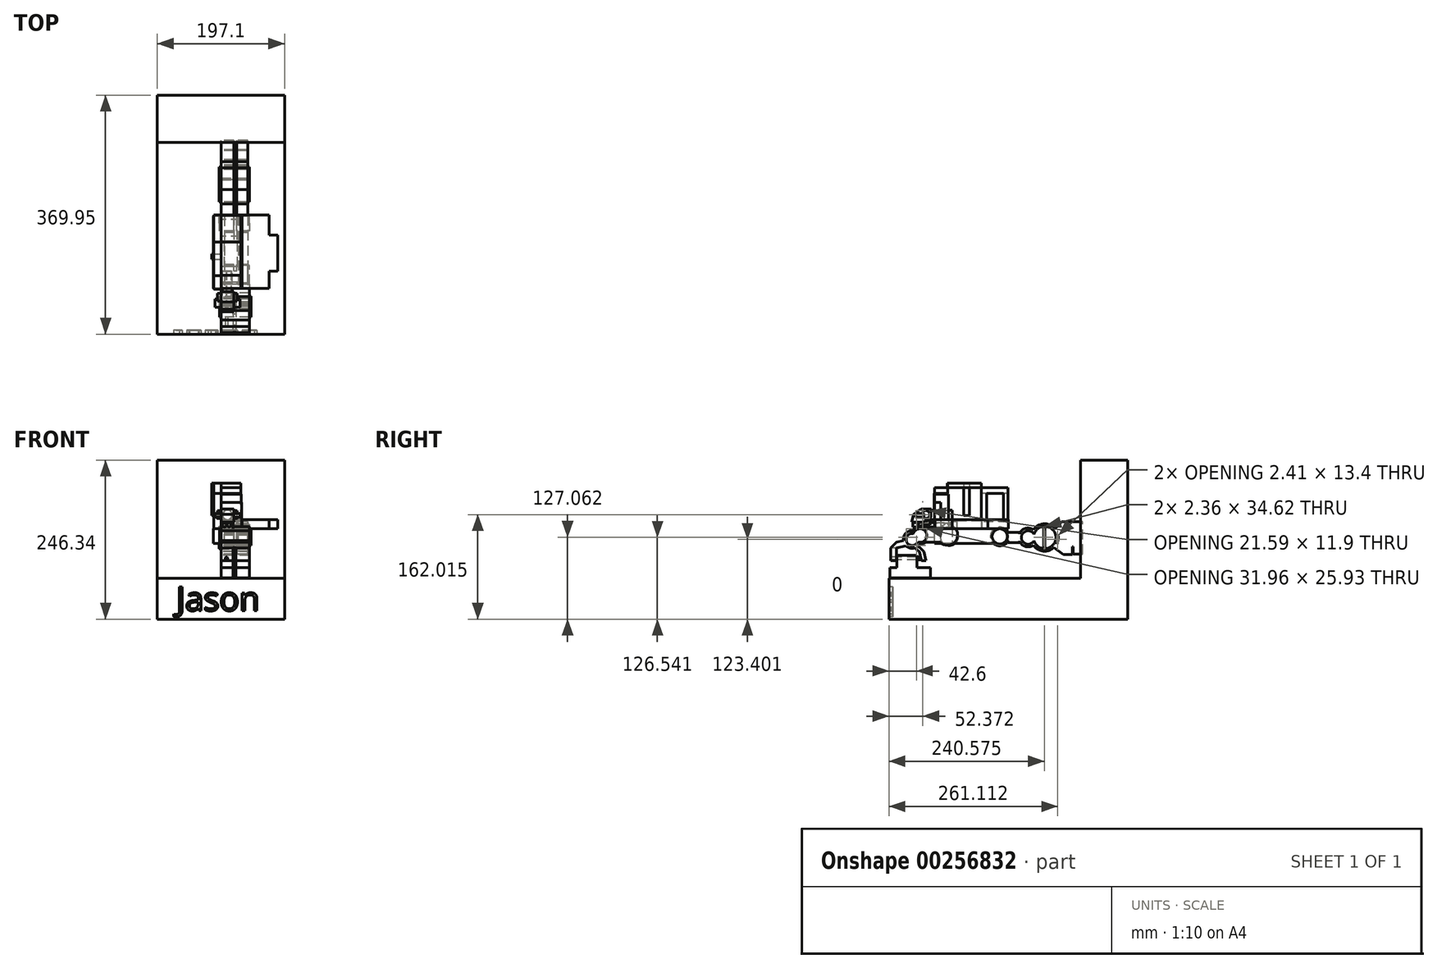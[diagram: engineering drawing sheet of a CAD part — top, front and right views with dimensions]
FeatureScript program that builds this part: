
annotation { "Feature Type Name" : "Feature", "Feature Type Description" : "" }
export const myFeature = defineFeature(function(context is Context, id is Id, definition is map)
    precondition{}
    {
        {
            var Q0;
            Q0=qCreatedBy(makeId("Right.planeOp"),FACE);
            var sketch = newSketch(context, id + "F0", { "sketchPlane" : qUnion([Q0])});
            skLineSegment(sketch, "E0", {"start": v(-32.05, 30.72) * mm, "end": v(-47.84, 30.72) * mm});
            skLineSegment(sketch, "E1", {"start": v(-47.84, 30.72) * mm, "end": v(-59.25, 22.22) * mm});
            skLineSegment(sketch, "E2", {"start": v(-59.25, 22.22) * mm, "end": v(-62.9, 10.56) * mm});
            skLineSegment(sketch, "E3", {"start": v(-62.9, 10.56) * mm, "end": v(-43.95, 10.56) * mm});
            skLineSegment(sketch, "E4", {"start": v(-43.95, 10.56) * mm, "end": v(-40.55, 13.23) * mm});
            skLineSegment(sketch, "E5", {"start": v(-40.55, 13.23) * mm, "end": v(-33.74, 13.23) * mm});
            skLineSegment(sketch, "E6", {"start": v(-33.74, 13.23) * mm, "end": v(-32.05, 30.72) * mm});
            skSolve(sketch);
        }
        {
            var Q0;
            Q0 = qSketchRegion(id + "F0", true);
            extrude(context, id + "F1", {"entities" : qUnion([Q0]), "depth" : 19.8 * mm});
        }
        {
            var Q0;
            Q0=qCreatedBy(makeId("Front.planeOp"),FACE);
            var sketch = newSketch(context, id + "F2", { "sketchPlane" : qUnion([Q0])});
            skCircle(sketch, "E7", {"center": v(9.48, 21.53) * mm, "radius": 7.5 * mm});
            skSolve(sketch);
        }
        {
            var Q0;
            Q0 = qSketchRegion(id + "F2", true);
            extrude(context, id + "F3", {"entities" : qUnion([Q0]), "operationType" : NewBodyOperationType.ADD, "depth" : 37.85 * mm});
        }
        {
            var Q0;
            Q0=qCreatedBy(makeId("Right.planeOp"),FACE);
            var sketch = newSketch(context, id + "F4", { "sketchPlane" : qUnion([Q0])});
            skLineSegment(sketch, "E8.bottom", {"start": v(-17.62, 40.64) * mm, "end": v(-27.05, 40.64) * mm});
            skLineSegment(sketch, "E8.top", {"start": v(-17.62, 0) * mm, "end": v(-27.05, 0) * mm});
            skLineSegment(sketch, "E8.left", {"start": v(-17.62, 40.64) * mm, "end": v(-17.62, 0) * mm});
            skLineSegment(sketch, "E8.right", {"start": v(-27.05, 40.64) * mm, "end": v(-27.05, 0) * mm});
            skSolve(sketch);
        }
        {
            var Q0;
            Q0 = qSketchRegion(id + "F4", true);
            extrude(context, id + "F5", {"entities" : qUnion([Q0]), "operationType" : NewBodyOperationType.ADD, "depth" : 31.5 * mm});
        }
        {
            var Q0;
            Q0=qCreatedBy(makeId("Top.planeOp"),FACE);
            var sketch = newSketch(context, id + "F6", { "sketchPlane" : qUnion([Q0])});
            skLineSegment(sketch, "E9.bottom", {"start": v(31.64, -17.62) * mm, "end": v(0, -17.62) * mm});
            skLineSegment(sketch, "E9.top", {"start": v(31.64, 7.04) * mm, "end": v(0, 7.04) * mm});
            skLineSegment(sketch, "E9.left", {"start": v(31.64, -17.62) * mm, "end": v(31.64, 7.04) * mm});
            skLineSegment(sketch, "E9.right", {"start": v(0, -17.62) * mm, "end": v(0, 7.04) * mm});
            skSolve(sketch);
        }
        {
            var Q0;
            Q0 = qSketchRegion(id + "F6", true);
            extrude(context, id + "F7", {"entities" : qUnion([Q0]), "operationType" : NewBodyOperationType.ADD, "depth" : 13.2 * mm});
        }
        {
            var Q0;
            Q0=qCreatedBy(makeId("Top.planeOp"),FACE);
            var sketch = newSketch(context, id + "F8", { "sketchPlane" : qUnion([Q0])});
            skLineSegment(sketch, "E10.bottom", {"start": v(31.4, 7.04) * mm, "end": v(25.12, 7.04) * mm});
            skLineSegment(sketch, "E10.top", {"start": v(31.4, 45.73) * mm, "end": v(25.12, 45.73) * mm});
            skLineSegment(sketch, "E10.left", {"start": v(31.4, 7.04) * mm, "end": v(31.4, 45.73) * mm});
            skLineSegment(sketch, "E10.right", {"start": v(25.12, 7.04) * mm, "end": v(25.12, 45.73) * mm});
            skSolve(sketch);
        }
        {
            var Q0;
            Q0 = qSketchRegion(id + "F8", true);
            extrude(context, id + "F9", {"entities" : qUnion([Q0]), "operationType" : NewBodyOperationType.ADD, "depth" : 12.95 * mm});
        }
        {
            var Q0;
            Q0=qCreatedBy(makeId("Top.planeOp"),FACE);
            var sketch = newSketch(context, id + "F10", { "sketchPlane" : qUnion([Q0])});
            skLineSegment(sketch, "E11.bottom", {"start": v(0, 7.28) * mm, "end": v(5.05, 7.28) * mm});
            skLineSegment(sketch, "E11.top", {"start": v(0, 46.45) * mm, "end": v(5.05, 46.45) * mm});
            skLineSegment(sketch, "E11.left", {"start": v(0, 7.28) * mm, "end": v(0, 46.45) * mm});
            skLineSegment(sketch, "E11.right", {"start": v(5.05, 7.28) * mm, "end": v(5.05, 46.45) * mm});
            skSolve(sketch);
        }
        {
            var Q0;
            Q0 = qSketchRegion(id + "F10", true);
            extrude(context, id + "F11", {"entities" : qUnion([Q0]), "depth" : 12.95 * mm});
        }
        {
            var Q0;
            Q0=qCreatedBy(makeId("Top.planeOp"),FACE);
            var sketch = newSketch(context, id + "F12", { "sketchPlane" : qUnion([Q0])});
            skLineSegment(sketch, "E12.bottom", {"start": v(31.16, 45.97) * mm, "end": v(0, 45.97) * mm});
            skLineSegment(sketch, "E12.top", {"start": v(31.16, 86.8) * mm, "end": v(0, 86.8) * mm});
            skLineSegment(sketch, "E12.left", {"start": v(31.16, 45.97) * mm, "end": v(31.16, 86.8) * mm});
            skLineSegment(sketch, "E12.right", {"start": v(0, 45.97) * mm, "end": v(0, 86.8) * mm});
            skSolve(sketch);
        }
        {
            var Q0;
            Q0 = qSketchRegion(id + "F12", true);
            extrude(context, id + "F13", {"entities" : qUnion([Q0]), "operationType" : NewBodyOperationType.ADD, "depth" : 13.97 * mm});
        }
        {
            var Q0;
            Q0=qCreatedBy(makeId("Top.planeOp"),FACE);
            var sketch = newSketch(context, id + "F14", { "sketchPlane" : qUnion([Q0])});
            skLineSegment(sketch, "E13.bottom", {"start": v(31.93, -26.75) * mm, "end": v(73.94, -26.75) * mm});
            skLineSegment(sketch, "E13.top", {"start": v(31.93, 86.9) * mm, "end": v(73.94, 86.9) * mm});
            skLineSegment(sketch, "E13.left", {"start": v(31.93, -26.75) * mm, "end": v(31.93, 86.9) * mm});
            skLineSegment(sketch, "E13.right", {"start": v(73.94, -26.75) * mm, "end": v(73.94, 86.9) * mm});
            skLineSegment(sketch, "E14.bottom", {"start": v(31.93, 0) * mm, "end": v(87.42, 0) * mm});
            skLineSegment(sketch, "E14.top", {"start": v(31.93, 55.68) * mm, "end": v(87.42, 55.68) * mm});
            skLineSegment(sketch, "E14.left", {"start": v(31.93, 0) * mm, "end": v(31.93, 55.68) * mm});
            skLineSegment(sketch, "E14.right", {"start": v(87.42, 0) * mm, "end": v(87.42, 55.68) * mm});
            skSolve(sketch);
        }
        {
            var Q0;
            Q0 = qSketchRegion(id + "F14", true);
            extrude(context, id + "F15", {"entities" : qUnion([Q0]), "depth" : 14.22 * mm});
        }
        {
            var Q0;
            Q0=qCreatedBy(makeId("Right.planeOp"),FACE);
            var sketch = newSketch(context, id + "F16", { "sketchPlane" : qUnion([Q0])});
            skLineSegment(sketch, "E15.bottom", {"start": v(86.49, 0) * mm, "end": v(-27.86, 0) * mm});
            skLineSegment(sketch, "E15.top", {"start": v(86.49, 54.6) * mm, "end": v(-27.86, 54.6) * mm});
            skLineSegment(sketch, "E15.left", {"start": v(86.49, 0) * mm, "end": v(86.49, 54.6) * mm});
            skLineSegment(sketch, "E15.right", {"start": v(-27.86, 0) * mm, "end": v(-27.86, 54.6) * mm});
            skLineSegment(sketch, "E16.bottom", {"start": v(45.18, 0) * mm, "end": v(-7.2, 0) * mm});
            skLineSegment(sketch, "E16.top", {"start": v(45.18, 70.73) * mm, "end": v(-7.2, 70.73) * mm});
            skLineSegment(sketch, "E16.left", {"start": v(45.18, 0) * mm, "end": v(45.18, 70.73) * mm});
            skLineSegment(sketch, "E16.right", {"start": v(-7.2, 0) * mm, "end": v(-7.2, 70.73) * mm});
            skSolve(sketch);
        }
        {
            var Q0;
            Q0 = qSketchRegion(id + "F16", true);
            extrude(context, id + "F17", {"entities" : qUnion([Q0]), "oppositeDirection" : true, "depth" : 11.43 * mm});
        }
        {
            var Q0;
            Q0=qCreatedBy(makeId("Top.planeOp"),FACE);
            var sketch = newSketch(context, id + "F18", { "sketchPlane" : qUnion([Q0])});
            skLineSegment(sketch, "E17.bottom", {"start": v(0, -5.7) * mm, "end": v(31, -5.7) * mm});
            skLineSegment(sketch, "E17.top", {"start": v(0, -26.85) * mm, "end": v(31, -26.85) * mm});
            skLineSegment(sketch, "E17.left", {"start": v(0, -5.7) * mm, "end": v(0, -26.85) * mm});
            skLineSegment(sketch, "E17.right", {"start": v(31, -5.7) * mm, "end": v(31, -26.85) * mm});
            skSolve(sketch);
        }
        {
            var Q0;
            Q0 = qSketchRegion(id + "F18", true);
            extrude(context, id + "F19", {"entities" : qUnion([Q0]), "depth" : 53.6 * mm});
        }
        {
            var Q0;
            Q0=qCreatedBy(makeId("Right.planeOp"),FACE);
            var sketch = newSketch(context, id + "F20", { "sketchPlane" : qUnion([Q0])});
            skLineSegment(sketch, "E18.bottom", {"start": v(45.1, 14.3) * mm, "end": v(53.66, 14.3) * mm});
            skLineSegment(sketch, "E18.top", {"start": v(45.1, 54.6) * mm, "end": v(53.66, 54.6) * mm});
            skLineSegment(sketch, "E18.left", {"start": v(45.1, 14.3) * mm, "end": v(45.1, 54.6) * mm});
            skLineSegment(sketch, "E18.right", {"start": v(53.66, 14.3) * mm, "end": v(53.66, 54.6) * mm});
            skLineSegment(sketch, "E19.bottom", {"start": v(79.86, 13.8) * mm, "end": v(86.4, 13.8) * mm});
            skLineSegment(sketch, "E19.top", {"start": v(79.86, 54.6) * mm, "end": v(86.4, 54.6) * mm});
            skLineSegment(sketch, "E19.left", {"start": v(79.86, 13.8) * mm, "end": v(79.86, 54.6) * mm});
            skLineSegment(sketch, "E19.right", {"start": v(86.4, 13.8) * mm, "end": v(86.4, 54.6) * mm});
            skLineSegment(sketch, "E20.bottom", {"start": v(86.4, 54.6) * mm, "end": v(45.1, 54.6) * mm});
            skLineSegment(sketch, "E20.top", {"start": v(86.4, 63.68) * mm, "end": v(45.1, 63.68) * mm});
            skLineSegment(sketch, "E20.left", {"start": v(86.4, 54.6) * mm, "end": v(86.4, 63.68) * mm});
            skLineSegment(sketch, "E20.right", {"start": v(45.1, 54.6) * mm, "end": v(45.1, 63.68) * mm});
            skLineSegment(sketch, "E21.bottom", {"start": v(45.1, 63.68) * mm, "end": v(-6.78, 63.68) * mm});
            skLineSegment(sketch, "E21.top", {"start": v(45.1, 70.73) * mm, "end": v(-6.78, 70.73) * mm});
            skLineSegment(sketch, "E21.left", {"start": v(45.1, 63.68) * mm, "end": v(45.1, 70.73) * mm});
            skLineSegment(sketch, "E21.right", {"start": v(-6.78, 63.68) * mm, "end": v(-6.78, 70.73) * mm});
            skLineSegment(sketch, "E22.bottom", {"start": v(-6.78, 63.68) * mm, "end": v(-26.93, 63.68) * mm});
            skLineSegment(sketch, "E22.top", {"start": v(-6.78, 54.6) * mm, "end": v(-26.93, 54.6) * mm});
            skLineSegment(sketch, "E22.left", {"start": v(-6.78, 63.68) * mm, "end": v(-6.78, 54.6) * mm});
            skLineSegment(sketch, "E22.right", {"start": v(-26.93, 63.68) * mm, "end": v(-26.93, 54.6) * mm});
            skSolve(sketch);
        }
        {
            var Q0;
            Q0 = qSketchRegion(id + "F20", true);
            extrude(context, id + "F21", {"entities" : qUnion([Q0]), "depth" : 30.23 * mm});
        }
        {
            var Q0;
            Q0=qCreatedBy(makeId("Top.planeOp"),FACE);
            var sketch = newSketch(context, id + "F22", { "sketchPlane" : qUnion([Q0])});
            skLineSegment(sketch, "E23.bottom", {"start": v(4.64, 84.64) * mm, "end": v(-12.48, 84.64) * mm});
            skLineSegment(sketch, "E23.top", {"start": v(4.64, -27.2) * mm, "end": v(-12.48, -27.2) * mm});
            skLineSegment(sketch, "E23.left", {"start": v(4.64, 84.64) * mm, "end": v(4.64, -27.2) * mm});
            skLineSegment(sketch, "E23.right", {"start": v(-12.48, 84.64) * mm, "end": v(-12.48, -27.2) * mm});
            skLineSegment(sketch, "E24.bottom", {"start": v(41.42, 85.14) * mm, "end": v(26.3, 85.14) * mm});
            skLineSegment(sketch, "E24.top", {"start": v(41.42, -27.2) * mm, "end": v(26.3, -27.2) * mm});
            skLineSegment(sketch, "E24.left", {"start": v(41.42, 85.14) * mm, "end": v(41.42, -27.2) * mm});
            skLineSegment(sketch, "E24.right", {"start": v(26.3, 85.14) * mm, "end": v(26.3, -27.2) * mm});
            skSolve(sketch);
        }
        {
            var Q0;
            Q0 = qSketchRegion(id + "F22", true);
            extrude(context, id + "F23", {"entities" : qUnion([Q0]), "oppositeDirection" : true, "depth" : 22.86 * mm});
        }
        {
            var Q0;
            Q0=qCreatedBy(makeId("Right.planeOp"),FACE);
            var sketch = newSketch(context, id + "F24", { "sketchPlane" : qUnion([Q0])});
            skLineSegment(sketch, "E25", {"start": v(-33.9, 12.8) * mm, "end": v(-33.9, 5.75) * mm});
            skLineSegment(sketch, "E26", {"start": v(-33.9, 5.75) * mm, "end": v(-47, 5.75) * mm});
            skLineSegment(sketch, "E27", {"start": v(-47, 5.75) * mm, "end": v(-52.04, 0) * mm});
            skLineSegment(sketch, "E28", {"start": v(-52.04, 0) * mm, "end": v(-52.04, 10.78) * mm});
            skLineSegment(sketch, "E29", {"start": v(-52.04, 10.78) * mm, "end": v(-33.9, 12.8) * mm});
            skSolve(sketch);
        }
        {
            var Q0;
            Q0 = qSketchRegion(id + "F24", true);
            extrude(context, id + "F25", {"entities" : qUnion([Q0]), "operationType" : NewBodyOperationType.ADD, "depth" : 18.29 * mm});
        }
        {
            var Q0;
            Q0=qCreatedBy(makeId("Right.planeOp"),FACE);
            var sketch = newSketch(context, id + "F26", { "sketchPlane" : qUnion([Q0])});
            skCircle(sketch, "E30", {"center": v(73.9, -11.89) * mm, "radius": 14.4 * mm});
            skCircle(sketch, "E31", {"center": v(-4.19, -11.38) * mm, "radius": 14.32 * mm});
            skLineSegment(sketch, "E32.bottom", {"start": v(86.78, -5.45) * mm, "end": v(104.12, -5.45) * mm});
            skLineSegment(sketch, "E32.top", {"start": v(86.78, -21.46) * mm, "end": v(104.12, -21.46) * mm});
            skLineSegment(sketch, "E32.left", {"start": v(86.78, -5.45) * mm, "end": v(86.78, -21.46) * mm});
            skLineSegment(sketch, "E32.right", {"start": v(104.12, -5.45) * mm, "end": v(104.12, -21.46) * mm});
            skCircle(sketch, "E33", {"center": v(117.72, -13.45) * mm, "radius": 14.62 * mm});
            skPoint(sketch, "E33.centerSnap0", {"position": v(104.12, -13.45) * mm});
            skCircle(sketch, "E34", {"center": v(143.41, -13.45) * mm, "radius": 21.13 * mm});
            skPoint(sketch, "E34.centerSnap0", {"position": v(86.78, -13.45) * mm});
            skLineSegment(sketch, "E35", {"start": v(159.7, 0) * mm, "end": v(169.6, 11.29) * mm});
            skLineSegment(sketch, "E36", {"start": v(169.6, 11.29) * mm, "end": v(187.74, 11.29) * mm});
            skLineSegment(sketch, "E37", {"start": v(187.74, 11.29) * mm, "end": v(187.74, 0) * mm});
            skLineSegment(sketch, "E38", {"start": v(187.74, 0) * mm, "end": v(171.12, 3) * mm});
            skLineSegment(sketch, "E39", {"start": v(171.12, 3) * mm, "end": v(164.23, -9.85) * mm});
            skLineSegment(sketch, "E40", {"start": v(164.23, -9.85) * mm, "end": v(162.13, -23.25) * mm});
            skLineSegment(sketch, "E41", {"start": v(162.13, -23.25) * mm, "end": v(173.63, -30.02) * mm});
            skLineSegment(sketch, "E42", {"start": v(173.63, -30.02) * mm, "end": v(186.17, -28.02) * mm});
            skLineSegment(sketch, "E43", {"start": v(186.17, -28.02) * mm, "end": v(186.17, -39.6) * mm});
            skLineSegment(sketch, "E44", {"start": v(186.17, -39.6) * mm, "end": v(172.63, -39.6) * mm});
            skLineSegment(sketch, "E45", {"start": v(172.63, -39.6) * mm, "end": v(157.55, -29.15) * mm});
            skLineSegment(sketch, "E46", {"start": v(157.55, -29.15) * mm, "end": v(159.7, 0) * mm});
            skLineSegment(sketch, "E47.bottom", {"start": v(187.74, 0) * mm, "end": v(173.63, 0) * mm});
            skLineSegment(sketch, "E47.top", {"start": v(187.74, -28.02) * mm, "end": v(173.63, -28.02) * mm});
            skLineSegment(sketch, "E47.left", {"start": v(187.74, 0) * mm, "end": v(187.74, -28.02) * mm});
            skLineSegment(sketch, "E47.right", {"start": v(173.63, 0) * mm, "end": v(173.63, -28.02) * mm});
            skLineSegment(sketch, "E48.bottom", {"start": v(187.74, 11.29) * mm, "end": v(202.35, 11.29) * mm});
            skLineSegment(sketch, "E48.top", {"start": v(187.74, -39.09) * mm, "end": v(202.35, -39.09) * mm});
            skLineSegment(sketch, "E48.left", {"start": v(187.74, 11.29) * mm, "end": v(187.74, -39.09) * mm});
            skLineSegment(sketch, "E48.right", {"start": v(202.35, 11.29) * mm, "end": v(202.35, -39.09) * mm});
            skSolve(sketch);
        }
        {
            var Q0;
            Q0 = qSketchRegion(id + "F26", true);
            extrude(context, id + "F27", {"entities" : qUnion([Q0]), "depth" : 40.9 * mm});
        }
        {
            var Q0;
            Q0=qCreatedBy(makeId("Right.planeOp"),FACE);
            var sketch = newSketch(context, id + "F28", { "sketchPlane" : qUnion([Q0])});
            skCircle(sketch, "E49", {"center": v(-7.37, -9.37) * mm, "radius": 16.03 * mm});
            skLineSegment(sketch, "E50.bottom", {"start": v(-20.39, 0) * mm, "end": v(-39.61, 0) * mm});
            skLineSegment(sketch, "E50.top", {"start": v(-20.39, -20.95) * mm, "end": v(-39.61, -20.95) * mm});
            skLineSegment(sketch, "E50.left", {"start": v(-20.39, 0) * mm, "end": v(-20.39, -20.95) * mm});
            skLineSegment(sketch, "E50.right", {"start": v(-39.61, 0) * mm, "end": v(-39.61, -20.95) * mm});
            skCircle(sketch, "E51", {"center": v(-49.69, -10.48) * mm, "radius": 13.58 * mm});
            skPoint(sketch, "E51.centerSnap0", {"position": v(-39.61, -10.48) * mm});
            skCircle(sketch, "E52", {"center": v(-61.86, -16.5) * mm, "radius": 13.76 * mm});
            skLineSegment(sketch, "E53", {"start": v(-52.57, -26.65) * mm, "end": v(-43.64, -35.56) * mm});
            skLineSegment(sketch, "E54", {"start": v(-43.64, -35.56) * mm, "end": v(-40.67, -49.28) * mm});
            skLineSegment(sketch, "E55", {"start": v(-40.67, -49.28) * mm, "end": v(-47.67, -49.28) * mm});
            skLineSegment(sketch, "E56", {"start": v(-47.67, -49.28) * mm, "end": v(-50.65, -35.56) * mm});
            skLineSegment(sketch, "E57", {"start": v(-50.65, -35.56) * mm, "end": v(-58.01, -29.7) * mm});
            skLineSegment(sketch, "E58", {"start": v(-75.48, -18.38) * mm, "end": v(-85.96, -20.65) * mm});
            skLineSegment(sketch, "E59", {"start": v(-85.96, -20.65) * mm, "end": v(-95.33, -29.7) * mm});
            skLineSegment(sketch, "E60", {"start": v(-95.33, -29.7) * mm, "end": v(-95.33, -49.28) * mm});
            skLineSegment(sketch, "E61", {"start": v(-95.33, -49.28) * mm, "end": v(-85.96, -49.28) * mm});
            skLineSegment(sketch, "E62", {"start": v(-85.96, -49.28) * mm, "end": v(-85.96, -35.56) * mm});
            skLineSegment(sketch, "E63", {"start": v(-85.96, -35.56) * mm, "end": v(-85.96, -29.7) * mm});
            skLineSegment(sketch, "E64", {"start": v(-85.96, -29.7) * mm, "end": v(-71.28, -26.52) * mm});
            skLineSegment(sketch, "E65.bottom", {"start": v(-54.73, -41.1) * mm, "end": v(-85.45, -41.1) * mm});
            skLineSegment(sketch, "E65.top", {"start": v(-54.73, -60.24) * mm, "end": v(-85.45, -60.24) * mm});
            skLineSegment(sketch, "E65.left", {"start": v(-54.73, -41.1) * mm, "end": v(-54.73, -60.24) * mm});
            skLineSegment(sketch, "E65.right", {"start": v(-85.45, -41.1) * mm, "end": v(-85.45, -60.24) * mm});
            skLineSegment(sketch, "E66.bottom", {"start": v(-33.57, -60.24) * mm, "end": v(-96.03, -60.24) * mm});
            skLineSegment(sketch, "E66.top", {"start": v(-33.57, -75.86) * mm, "end": v(-96.03, -75.86) * mm});
            skLineSegment(sketch, "E66.left", {"start": v(-33.57, -60.24) * mm, "end": v(-33.57, -75.86) * mm});
            skLineSegment(sketch, "E66.right", {"start": v(-96.03, -60.24) * mm, "end": v(-96.03, -75.86) * mm});
            skSolve(sketch);
        }
        {
            var Q0;
            Q0 = qSketchRegion(id + "F28", true);
            extrude(context, id + "F29", {"entities" : qUnion([Q0]), "depth" : 43.43 * mm});
        }
        {
            var Q0;
            Q0=qCreatedBy(makeId("Front.planeOp"),FACE);
            var sketch = newSketch(context, id + "F30", { "sketchPlane" : qUnion([Q0])});
            skCircle(sketch, "E67", {"center": v(4.88, 5.95) * mm, "radius": 3.27 * mm});
            skCircle(sketch, "E68", {"center": v(12.17, 6.2) * mm, "radius": 3.24 * mm});
            skSolve(sketch);
        }
        {
            var Q0;
            Q0 = qSketchRegion(id + "F30", true);
            extrude(context, id + "F31", {"entities" : qUnion([Q0]), "depth" : 60.45 * mm});
        }
        {
            var Q0;
            Q0=qCreatedBy(makeId("Right.planeOp"),FACE);
            var sketch = newSketch(context, id + "F32", { "sketchPlane" : qUnion([Q0])});
            skCircle(sketch, "E69", {"center": v(-40.48, 22) * mm, "radius": 6.02 * mm});
            skSolve(sketch);
        }
        {
            var Q0;
            Q0 = qSketchRegion(id + "F32", true);
            extrude(context, id + "F33", {"entities" : qUnion([Q0]), "operationType" : NewBodyOperationType.ADD, "depth" : 24.38 * mm, "hasSecondDirection" : true, "secondDirectionOppositeDirection" : true, "secondDirectionDepth" : 6.1 * mm});
        }
        {
            var Q0;
            Q0=qCreatedBy(makeId("Right.planeOp"),FACE);
            var sketch = newSketch(context, id + "F34", { "sketchPlane" : qUnion([Q0])});
            skLineSegment(sketch, "E70.bottom", {"start": v(-43.3, 23.51) * mm, "end": v(-56.2, 23.51) * mm});
            skLineSegment(sketch, "E70.top", {"start": v(-43.3, 18.14) * mm, "end": v(-56.2, 18.14) * mm});
            skLineSegment(sketch, "E70.left", {"start": v(-43.3, 23.51) * mm, "end": v(-43.3, 18.14) * mm});
            skLineSegment(sketch, "E70.right", {"start": v(-56.2, 23.51) * mm, "end": v(-56.2, 18.14) * mm});
            skSolve(sketch);
        }
        {
            var Q0;
            Q0 = qSketchRegion(id + "F34", true);
            extrude(context, id + "F35", {"entities" : qUnion([Q0]), "operationType" : NewBodyOperationType.ADD, "depth" : 28.96 * mm, "hasSecondDirection" : true, "secondDirectionOppositeDirection" : true, "secondDirectionDepth" : 9.65 * mm});
        }
        {
            var Q0;
            Q0=makeQuery(id+"F29.opExtrude","CAP_FACE",FACE,{"disambiguationData":[OSD([sQuery(id+"F28.wireOp",EDGE,"E49"),sQuery(id+"F28.wireOp",EDGE,"E50.bottom"),sQuery(id+"F28.wireOp",EDGE,"E50.top"),sQuery(id+"F28.wireOp",EDGE,"E50.left"),sQuery(id+"F28.wireOp",EDGE,"E50.right"),sQuery(id+"F28.wireOp",EDGE,"E51"),sQuery(id+"F28.wireOp",EDGE,"E52"),sQuery(id+"F28.wireOp",EDGE,"E53"),sQuery(id+"F28.wireOp",EDGE,"E54"),sQuery(id+"F28.wireOp",EDGE,"E55"),sQuery(id+"F28.wireOp",EDGE,"E56"),sQuery(id+"F28.wireOp",EDGE,"E57"),sQuery(id+"F28.wireOp",EDGE,"E58"),sQuery(id+"F28.wireOp",EDGE,"E59"),sQuery(id+"F28.wireOp",EDGE,"E60"),sQuery(id+"F28.wireOp",EDGE,"E61"),sQuery(id+"F28.wireOp",EDGE,"E62"),sQuery(id+"F28.wireOp",EDGE,"E63"),sQuery(id+"F28.wireOp",EDGE,"E64")])],"isStart":false});
            var sketch = newSketch(context, id + "F36", { "sketchPlane" : qUnion([Q0])});
            skCircle(sketch, "E71", {"center": v(-61.86, -16.5) * mm, "radius": 9.35 * mm});
            skCircle(sketch, "E72", {"center": v(-49.69, -10.48) * mm, "radius": 10.59 * mm});
            skSolve(sketch);
        }
        {
            var Q0;
            Q0 = qSketchRegion(id + "F36", true);
            extrude(context, id + "F37", {"entities" : qUnion([Q0]), "operationType" : NewBodyOperationType.ADD, "depth" : 2.54 * mm, "hasSecondDirection" : true, "secondDirectionOppositeDirection" : true, "secondDirectionDepth" : 46.23 * mm});
        }
        {
            var Q0;
            Q0=makeQuery(id+"F27.opExtrude","CAP_FACE",FACE,{"disambiguationData":[OSD([sQuery(id+"F26.wireOp",EDGE,"E30"),sQuery(id+"F26.wireOp",EDGE,"E32.bottom"),sQuery(id+"F26.wireOp",EDGE,"E32.top"),sQuery(id+"F26.wireOp",EDGE,"E32.left"),sQuery(id+"F26.wireOp",EDGE,"E32.right"),sQuery(id+"F26.wireOp",EDGE,"E33"),sQuery(id+"F26.wireOp",EDGE,"E34"),sQuery(id+"F26.wireOp",EDGE,"E35"),sQuery(id+"F26.wireOp",EDGE,"E36"),sQuery(id+"F26.wireOp",EDGE,"E40"),sQuery(id+"F26.wireOp",EDGE,"E43"),sQuery(id+"F26.wireOp",EDGE,"E44"),sQuery(id+"F26.wireOp",EDGE,"E45"),sQuery(id+"F26.wireOp",EDGE,"E47.top"),sQuery(id+"F26.wireOp",EDGE,"E48.bottom"),sQuery(id+"F26.wireOp",EDGE,"E48.top"),sQuery(id+"F26.wireOp",EDGE,"E48.left"),sQuery(id+"F26.wireOp",EDGE,"E48.right")])],"isStart":false});
            var sketch = newSketch(context, id + "F38", { "sketchPlane" : qUnion([Q0])});
            skCircle(sketch, "E73", {"center": v(143.41, -13.45) * mm, "radius": 17.36 * mm});
            skCircle(sketch, "E74", {"center": v(117.72, -13.45) * mm, "radius": 10.34 * mm});
            skCircle(sketch, "E75", {"center": v(73.9, -11.89) * mm, "radius": 11.88 * mm});
            skSolve(sketch);
        }
        {
            var Q0;
            Q0 = qSketchRegion(id + "F38", true);
            extrude(context, id + "F39", {"entities" : qUnion([Q0]), "depth" : 2.8 * mm, "hasSecondDirection" : true, "secondDirectionOppositeDirection" : true, "secondDirectionDepth" : 43.94 * mm});
        }
        {
            var Q0;
            Q0=makeQuery(id+"F39.opExtrude","CAP_FACE",FACE,{"disambiguationData":[OSD([sQuery(id+"F38.wireOp",EDGE,"E73"),sQuery(id+"F38.wireOp",EDGE,"E74")])],"isStart":false});
            var sketch = newSketch(context, id + "F40", { "sketchPlane" : qUnion([Q0])});
            skLineSegment(sketch, "E76", {"start": v(141.61, 3.82) * mm, "end": v(141.61, -30.72) * mm});
            skLineSegment(sketch, "E77", {"start": v(143.98, 3.9) * mm, "end": v(143.98, -30.72) * mm});
            skLineSegment(sketch, "E78", {"start": v(141.61, 3.82) * mm, "end": v(143.98, 3.9) * mm});
            skLineSegment(sketch, "E79", {"start": v(143.98, -30.72) * mm, "end": v(141.61, -30.72) * mm});
            skSolve(sketch);
        }
        {
            var Q0;
            Q0 = qSketchRegion(id + "F40", true);
            extrude(context, id + "F41", {"entities" : qUnion([Q0]), "operationType" : NewBodyOperationType.REMOVE, "oppositeDirection" : true, "depth" : 63.75 * mm});
        }
        {
            var Q0;
            Q0=makeQuery(id+"F37.opExtrude","CAP_FACE",FACE,{"disambiguationData":[OSD([sQuery(id+"F36.wireOp",EDGE,"E71"),sQuery(id+"F36.wireOp",EDGE,"E72")])],"isStart":true});
            var sketch = newSketch(context, id + "F42", { "sketchPlane" : qUnion([Q0])});
            skLineSegment(sketch, "E80", {"start": v(40.7, -16.06) * mm, "end": v(55.23, -1.46) * mm});
            skLineSegment(sketch, "E81", {"start": v(55.23, -1.46) * mm, "end": v(56.98, -2.8) * mm});
            skLineSegment(sketch, "E82", {"start": v(56.98, -2.8) * mm, "end": v(42.05, -17.8) * mm});
            skLineSegment(sketch, "E83", {"start": v(42.05, -17.8) * mm, "end": v(40.7, -16.06) * mm});
            skSolve(sketch);
        }
        {
            var Q0;
            Q0=makeQuery(id+"F42.imprint","IMPRINT",FACE,{"disambiguationData":[TD([[makeQuery(id+"F42.imprint","IMPRINT",EDGE,{"derivedFrom":sQuery(id+"F42.wireOp",EDGE,"E80")}),-1.0]])]});
            extrude(context, id + "F43", {"entities" : qUnion([Q0]), "operationType" : NewBodyOperationType.ADD, "oppositeDirection" : true, "depth" : 36.07 * mm});
        }
        {
            var Q0;
            Q0=qCreatedBy(makeId("Right.planeOp"),FACE);
            var sketch = newSketch(context, id + "F44", { "sketchPlane" : qUnion([Q0])});
            skLineSegment(sketch, "E84.bottom", {"start": v(26.64, 70.67) * mm, "end": v(18.16, 70.67) * mm});
            skLineSegment(sketch, "E84.top", {"start": v(26.64, 20.64) * mm, "end": v(18.16, 20.64) * mm});
            skLineSegment(sketch, "E84.left", {"start": v(26.64, 70.67) * mm, "end": v(26.64, 20.64) * mm});
            skLineSegment(sketch, "E84.right", {"start": v(18.16, 70.67) * mm, "end": v(18.16, 20.64) * mm});
            skSolve(sketch);
        }
        {
            var Q0;
            Q0 = qSketchRegion(id + "F44", true);
            extrude(context, id + "F45", {"entities" : qUnion([Q0]), "oppositeDirection" : true, "depth" : 14.48 * mm});
        }
        {
            var Q0;
            Q0=qCreatedBy(makeId("Front.planeOp"),FACE);
            var sketch = newSketch(context, id + "F46", { "sketchPlane" : qUnion([Q0])});
            skLineSegment(sketch, "E85.bottom", {"start": v(18, -29.26) * mm, "end": v(22.6, -29.26) * mm});
            skLineSegment(sketch, "E85.top", {"start": v(18, -77.82) * mm, "end": v(22.6, -77.82) * mm});
            skLineSegment(sketch, "E85.left", {"start": v(18, -29.26) * mm, "end": v(18, -77.82) * mm});
            skLineSegment(sketch, "E85.right", {"start": v(22.6, -29.26) * mm, "end": v(22.6, -77.82) * mm});
            skSolve(sketch);
        }
        {
            var Q0;
            Q0 = qSketchRegion(id + "F46", true);
            extrude(context, id + "F47", {"entities" : qUnion([Q0]), "operationType" : NewBodyOperationType.REMOVE, "depth" : 115.32 * mm});
        }
        {
            var Q0;
            Q0=qCreatedBy(makeId("Front.planeOp"),FACE);
            var sketch = newSketch(context, id + "F48", { "sketchPlane" : qUnion([Q0])});
            skLineSegment(sketch, "E86.bottom", {"start": v(23.82, 11.3) * mm, "end": v(19.2, 11.3) * mm});
            skLineSegment(sketch, "E86.top", {"start": v(23.82, -39.7) * mm, "end": v(19.2, -39.7) * mm});
            skLineSegment(sketch, "E86.left", {"start": v(23.82, 11.3) * mm, "end": v(23.82, -39.7) * mm});
            skLineSegment(sketch, "E86.right", {"start": v(19.2, 11.3) * mm, "end": v(19.2, -39.7) * mm});
            skSolve(sketch);
        }
        {
            var Q0;
            Q0 = qSketchRegion(id + "F48", true);
            extrude(context, id + "F49", {"entities" : qUnion([Q0]), "operationType" : NewBodyOperationType.REMOVE, "oppositeDirection" : true, "depth" : 206.5 * mm});
        }
        {
            var Q0;
            {var subQ1=sQuery(id+"F28.wireOp",EDGE,"E60");Q0=makeQuery(id+"F47.boolean.opBoolean","SPLIT",FACE,{"disambiguationData":[TD([makeQuery(id+"F47.opExtrude","SWEPT_FACE",FACE,{"disambiguationData":[OSD([sQuery(id+"F46.wireOp",EDGE,"E85.left")])]})])],"derivedFrom":makeQuery(id+"F29.opExtrude","SWEPT_FACE",FACE,{"disambiguationData":[OSD([subQ1])]})});}
            var sketch = newSketch(context, id + "F50", { "sketchPlane" : qUnion([Q0])});
            skCircle(sketch, "E87", {"center": v(8.04, -46.01) * mm, "radius": 2.17 * mm});
            skSolve(sketch);
        }
        {
            var Q0;
            Q0 = qSketchRegion(id + "F50", true);
            extrude(context, id + "F51", {"entities" : qUnion([Q0]), "oppositeDirection" : true, "depth" : 48 * mm});
        }
        {
            var Q0;
            Q0=qCreatedBy(makeId("Right.planeOp"),FACE);
            var sketch = newSketch(context, id + "F52", { "sketchPlane" : qUnion([Q0])});
            skLineSegment(sketch, "E88.bottom", {"start": v(-97.78, -76.59) * mm, "end": v(207.04, -76.59) * mm});
            skLineSegment(sketch, "E88.top", {"start": v(-97.78, -139.95) * mm, "end": v(207.04, -139.95) * mm});
            skLineSegment(sketch, "E88.left", {"start": v(-97.78, -76.59) * mm, "end": v(-97.78, -139.95) * mm});
            skLineSegment(sketch, "E88.right", {"start": v(207.04, -76.59) * mm, "end": v(207.04, -139.95) * mm});
            skLineSegment(sketch, "E89.bottom", {"start": v(207.04, -139.95) * mm, "end": v(272.17, -139.95) * mm});
            skLineSegment(sketch, "E89.top", {"start": v(207.04, 106.4) * mm, "end": v(272.17, 106.4) * mm});
            skLineSegment(sketch, "E89.left", {"start": v(207.04, -139.95) * mm, "end": v(207.04, 106.4) * mm});
            skLineSegment(sketch, "E89.right", {"start": v(272.17, -139.95) * mm, "end": v(272.17, 106.4) * mm});
            skLineSegment(sketch, "E90.bottom", {"start": v(207.04, 106.4) * mm, "end": v(199.07, 106.4) * mm});
            skLineSegment(sketch, "E90.top", {"start": v(207.04, -76.59) * mm, "end": v(199.07, -76.59) * mm});
            skLineSegment(sketch, "E90.left", {"start": v(207.04, 106.4) * mm, "end": v(207.04, -76.59) * mm});
            skLineSegment(sketch, "E90.right", {"start": v(199.07, 106.4) * mm, "end": v(199.07, -76.59) * mm});
            skSolve(sketch);
        }
        {
            var Q0;
            Q0 = qSketchRegion(id + "F52", true);
            extrude(context, id + "F53", {"entities" : qUnion([Q0]), "depth" : 98.04 * mm, "hasSecondDirection" : true, "secondDirectionOppositeDirection" : true, "secondDirectionDepth" : 99.06 * mm});
        }
        {
            var Q0;
            Q0=makeQuery(id+"F53.opExtrude","SWEPT_FACE",FACE,{"disambiguationData":[OSD([sQuery(id+"F52.wireOp",EDGE,"E88.left")])]});
            var sketch = newSketch(context, id + "F54", { "sketchPlane" : qUnion([Q0])});
            skText(sketch, "E91", { "text": "Jason", "fontName": "OpenSans-Regular.ttf"});
            const initialGuessF54  = {"E91": [-0.06959, -0.12687, 1, 0, 0.0369]};
            skSetInitialGuess(sketch, initialGuessF54);
            skSolve(sketch);
        }
        {
            var Q0;
            Q0 = qSketchRegion(id + "F54", true);
            extrude(context, id + "F55", {"entities" : qUnion([Q0]), "operationType" : NewBodyOperationType.REMOVE, "oppositeDirection" : true, "depth" : 5.84 * mm});
        }
    });
